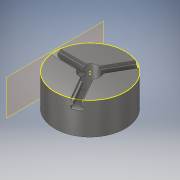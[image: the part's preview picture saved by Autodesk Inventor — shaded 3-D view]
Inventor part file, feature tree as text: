
AUTODESK INVENTOR PART (.ipt)
format: ipt  version: 2018 (Build 220112000, 112)  size: 262,656 bytes
history: native  units: in
note: dims shown in document units (in); Inventor stores cm internally (conversion verified against a paired STEP export)
features: sketch x13, extrude x11, plane x1, pattern_circular x1, projected_geometry x1
ambient origin geometry x8: Origin, YZ Plane, XZ Plane, XY Plane, X Axis, Y Axis, Z Axis, Center Point
bodies: Solid1 (feature_tree)
feature tree (27):
  extrude  "Extrusion1"  Depth=3.5787in
  extrude  "Extrusion2"  Depth=3.5787in
  sketch  "Sketch3"  dims[d13=1.1811in d15=360.0deg d17=0.2827in d18=0.0in]
  extrude  "Extrusion6"  Depth=0.2827in TaperAngle=0.0deg
  extrude  "Extrusion7"  Depth=0.3937in TaperAngle=0.0deg
  extrude  "Extrusion8"  Depth=0.3937in TaperAngle=0.0deg
  extrude  "Extrusion9"  Depth=0.3748in TaperAngle=0.0deg
  extrude  "Extrusion10"  Depth=0.3937in TaperAngle=0.0deg
  sketch  "Sketch12"  dims[d43=1.1811in d44=360.0deg d48=1.1811in d50=360.0deg]
  sketch  "Sketch13"  dims[d52=1.9685in d53=0.0in]
  plane  "Work Plane10"
  extrude  "Extrusion11"  Depth=1.1811in TaperAngle=360.0deg
  extrude  "Extrusion12"  [1 undecoded]
  extrude  "Extrusion13"  [1 undecoded]
  pattern_circular  "Circular Pattern1"  [2 undecoded]
  extrude  "Extrusion14"  [1 undecoded]
  sketch  "Sketch1"  dims[d1=3.5787in d2=0.0in d3=2.1701in]
  sketch  "Sketch2"  dims[d4=3.5787in d5=0.0in d6=0.5256in]
  sketch  "Sketch7"  dims[d19=0.3937in d20=0.0in d21=0.3937in d22=0.0in]
  sketch  "Sketch8"  dims[d23=0.3937in d24=0.0in d25=0.3937in d26=0.0in]
  sketch  "Sketch10"  dims[d36=0.3748in d37=2.9365in d38=0.0in]
  sketch  "Sketch11"  dims[d39=2.9365in d40=0.0in d41=0.3937in d42=0.0in]
  projected_geometry  "Projected Loop1"
  sketch  "Sketch16"
  sketch  "Sketch18"
  sketch  "Sketch20"
  sketch  "Sketch21"
note: 5 required parameter values undecoded (feature->parameter linkage not recoverable at this tier; creation-order binding heuristic only, values carry confidence <= 0.55)
